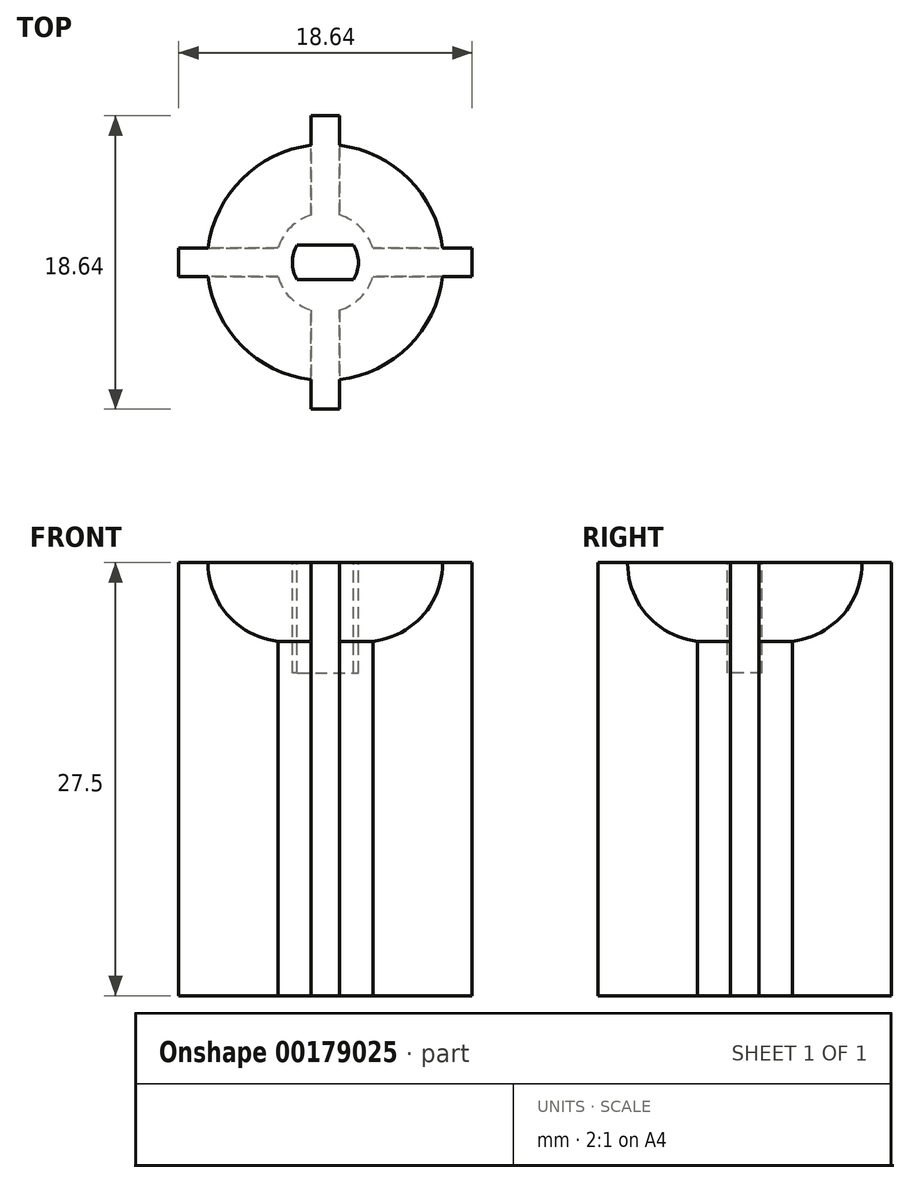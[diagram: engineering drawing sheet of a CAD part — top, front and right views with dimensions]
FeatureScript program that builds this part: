
annotation { "Feature Type Name" : "Feature", "Feature Type Description" : "" }
export const myFeature = defineFeature(function(context is Context, id is Id, definition is map)
    precondition{}
    {
        {
            var Q0;
            Q0=qCreatedBy(makeId("Top.planeOp"),FACE);
            var sketch = newSketch(context, id + "F0", { "sketchPlane" : qUnion([Q0])});
            skCircle(sketch, "E0", {"center": v(0, 0) * mm, "radius": 3.15 * mm});
            skLineSegment(sketch, "E1", {"start": v(-3.02, 0.9) * mm, "end": v(-9.32, 0.9) * mm});
            skLineSegment(sketch, "E2", {"start": v(-9.32, 0.9) * mm, "end": v(-9.32, -0.9) * mm});
            skLineSegment(sketch, "E3", {"start": v(-9.32, -0.9) * mm, "end": v(-3.02, -0.9) * mm});
            skLineSegment(sketch, "E4.1.0", {"start": v(-0.9, -3.02) * mm, "end": v(-0.9, -9.32) * mm});
            skLineSegment(sketch, "E4.1.1", {"start": v(-0.9, -9.32) * mm, "end": v(0.9, -9.32) * mm});
            skLineSegment(sketch, "E4.1.2", {"start": v(0.9, -9.32) * mm, "end": v(0.9, -3.02) * mm});
            skLineSegment(sketch, "E4.2.0", {"start": v(3.02, -0.9) * mm, "end": v(9.32, -0.9) * mm});
            skLineSegment(sketch, "E4.2.1", {"start": v(9.32, -0.9) * mm, "end": v(9.32, 0.9) * mm});
            skLineSegment(sketch, "E4.2.2", {"start": v(9.32, 0.9) * mm, "end": v(3.02, 0.9) * mm});
            skLineSegment(sketch, "E4.3.0", {"start": v(0.9, 3.02) * mm, "end": v(0.9, 9.32) * mm});
            skLineSegment(sketch, "E4.3.1", {"start": v(0.9, 9.32) * mm, "end": v(-0.9, 9.32) * mm});
            skLineSegment(sketch, "E4.3.2", {"start": v(-0.9, 9.32) * mm, "end": v(-0.9, 3.02) * mm});
            skSolve(sketch);
        }
        {
            var Q0;
            Q0=qSketchRegion(id+"F0",true);
            extrude(context, id + "F1", {"entities" : qUnion([Q0]), "depth" : 25 * mm});
        }
        {
            var Q0;
            Q0=makeQuery(id+"F1.opExtrude","CAP_FACE",FACE,{"disambiguationData":[OSD([sQuery(id+"F0.wireOp",EDGE,"E0"),sQuery(id+"F0.wireOp",EDGE,"E1"),sQuery(id+"F0.wireOp",EDGE,"E2"),sQuery(id+"F0.wireOp",EDGE,"E3"),sQuery(id+"F0.wireOp",EDGE,"3edc4b27-075a-45ef-aea2-eed3a7496e3e2.MirrorCS"),sQuery(id+"F0.wireOp",EDGE,"3edc4b27-075a-45ef-aea2-eed3a7496e3e4.MirrorCS"),sQuery(id+"F0.wireOp",EDGE,"q4PIojLU-buq7-G7pm-UIdF-VrHVZa9xzF9O")])],"isStart":false});
            var sketch = newSketch(context, id + "F2", { "sketchPlane" : qUnion([Q0])});
            skCircle(sketch, "E5", {"center": v(0, 0) * mm, "radius": 2.1 * mm});
            skLineSegment(sketch, "E6", {"start": v(-1.79, 1.1) * mm, "end": v(1.79, 1.1) * mm});
            skLineSegment(sketch, "E7", {"start": v(-1.79, -1.1) * mm, "end": v(1.79, -1.1) * mm});
            skSolve(sketch);
        }
        {
            var Q0;
            {var subQ0=sQuery(id+"F2.wireOp",EDGE,"E6");Q0=makeQuery(id+"F2.imprint","IMPRINT",FACE,{"disambiguationData":[TD([[makeQuery(id+"F2.imprint","IMPRINT",EDGE,{"derivedFrom":subQ0}),-1.0]])]});}
            extrude(context, id + "F3", {"entities" : qUnion([Q0]), "operationType" : NewBodyOperationType.REMOVE, "oppositeDirection" : true, "depth" : 7 * mm});
        }
        {
            var Q0;
            Q0=qCreatedBy(makeId("Front.planeOp"),FACE);
            cPlane(context, id + "F4", {"entities" : qUnion([Q0]), "cplaneType" : CPlaneType.OFFSET, "offset" : 3.25 * mm, "width" : 150 * mm, "height" : 150 * mm});
        }
        {
            var Q0;
            Q0=makeQuery(id+"F1.opExtrude","CAP_FACE",FACE,{"disambiguationData":[OSD([sQuery(id+"F0.wireOp",EDGE,"E0"),sQuery(id+"F0.wireOp",EDGE,"E1"),sQuery(id+"F0.wireOp",EDGE,"E2"),sQuery(id+"F0.wireOp",EDGE,"E3"),sQuery(id+"F0.wireOp",EDGE,"E4.1.0"),sQuery(id+"F0.wireOp",EDGE,"E4.1.1"),sQuery(id+"F0.wireOp",EDGE,"E4.1.2"),sQuery(id+"F0.wireOp",EDGE,"E4.2.0"),sQuery(id+"F0.wireOp",EDGE,"E4.2.1"),sQuery(id+"F0.wireOp",EDGE,"E4.2.2"),sQuery(id+"F0.wireOp",EDGE,"E4.3.0"),sQuery(id+"F0.wireOp",EDGE,"E4.3.1"),sQuery(id+"F0.wireOp",EDGE,"E4.3.2")])],"isStart":false});
            var sketch = newSketch(context, id + "F5", { "sketchPlane" : qUnion([Q0])});
            skCircle(sketch, "E8", {"center": v(0, 0) * mm, "radius": 7.5 * mm});
            skSolve(sketch);
        }
        {
            var Q0;
            {var subQ4=sQuery(id+"F0.wireOp",EDGE,"E1");var subQ7=sQuery(id+"F0.wireOp",EDGE,"E0");var subQ8=makeQuery(id+"F1.opExtrude","CAP_EDGE",EDGE,{"disambiguationData":[OSD([subQ7]),TDD([makeQuery(id+"F0.imprint","IMPRINT",EDGE,{"disambiguationData":[TD([[makeQuery(id+"F0.imprint","INTERSECT",VERTEX,{"derivedFrom":[subQ7,subQ4]}),1.0]])],"derivedFrom":subQ7})])],"isStart":false});Q0=makeQuery(id+"F5.imprint","IMPRINT",FACE,{"disambiguationData":[TD([[makeQuery(id+"F5.imprint","IMPRINT",EDGE,{"derivedFrom":subQ8}),-1.0]])]});}
            var Q1;
            {var subQ1=sQuery(id+"F0.wireOp",EDGE,"E3");var subQ7=sQuery(id+"F0.wireOp",EDGE,"E0");var subQ8=makeQuery(id+"F1.opExtrude","CAP_EDGE",EDGE,{"disambiguationData":[OSD([subQ7]),TDD([makeQuery(id+"F0.imprint","IMPRINT",EDGE,{"disambiguationData":[TD([[makeQuery(id+"F0.imprint","INTERSECT",VERTEX,{"derivedFrom":[subQ7,subQ1]}),-1.0]])],"derivedFrom":subQ7})])],"isStart":false});Q1=makeQuery(id+"F5.imprint","IMPRINT",FACE,{"disambiguationData":[TD([[makeQuery(id+"F5.imprint","IMPRINT",EDGE,{"derivedFrom":subQ8}),-1.0]])]});}
            var Q2;
            {var subQ1=sQuery(id+"F0.wireOp",EDGE,"E4.1.2");var subQ7=sQuery(id+"F0.wireOp",EDGE,"E0");var subQ8=makeQuery(id+"F1.opExtrude","CAP_EDGE",EDGE,{"disambiguationData":[OSD([subQ7]),TDD([makeQuery(id+"F0.imprint","IMPRINT",EDGE,{"disambiguationData":[TD([[makeQuery(id+"F0.imprint","INTERSECT",VERTEX,{"derivedFrom":[subQ7,subQ1]}),-1.0]])],"derivedFrom":subQ7})])],"isStart":false});Q2=makeQuery(id+"F5.imprint","IMPRINT",FACE,{"disambiguationData":[TD([[makeQuery(id+"F5.imprint","IMPRINT",EDGE,{"derivedFrom":subQ8}),-1.0]])]});}
            var Q3;
            {var subQ4=sQuery(id+"F0.wireOp",EDGE,"E4.2.2");var subQ7=sQuery(id+"F0.wireOp",EDGE,"E0");var subQ8=makeQuery(id+"F1.opExtrude","CAP_EDGE",EDGE,{"disambiguationData":[OSD([subQ7]),TDD([makeQuery(id+"F0.imprint","IMPRINT",EDGE,{"disambiguationData":[TD([[makeQuery(id+"F0.imprint","INTERSECT",VERTEX,{"derivedFrom":[subQ7,subQ4]}),-1.0]])],"derivedFrom":subQ7})])],"isStart":false});Q3=makeQuery(id+"F5.imprint","IMPRINT",FACE,{"disambiguationData":[TD([[makeQuery(id+"F5.imprint","IMPRINT",EDGE,{"derivedFrom":subQ8}),-1.0]])]});}
            extrude(context, id + "F6", {"entities" : qUnion([Q0, Q1, Q2, Q3]), "operationType" : NewBodyOperationType.ADD, "oppositeDirection" : true, "depth" : 5 * mm});
        }
        {
            var Q0;
            Q0=makeQuery(id+"F1.opExtrude","CAP_FACE",FACE,{"disambiguationData":[OSD([sQuery(id+"F0.wireOp",EDGE,"E0"),sQuery(id+"F0.wireOp",EDGE,"E1"),sQuery(id+"F0.wireOp",EDGE,"E2"),sQuery(id+"F0.wireOp",EDGE,"E3"),sQuery(id+"F0.wireOp",EDGE,"E4.1.0"),sQuery(id+"F0.wireOp",EDGE,"E4.1.1"),sQuery(id+"F0.wireOp",EDGE,"E4.1.2"),sQuery(id+"F0.wireOp",EDGE,"E4.2.0"),sQuery(id+"F0.wireOp",EDGE,"E4.2.1"),sQuery(id+"F0.wireOp",EDGE,"E4.2.2"),sQuery(id+"F0.wireOp",EDGE,"E4.3.0"),sQuery(id+"F0.wireOp",EDGE,"E4.3.1"),sQuery(id+"F0.wireOp",EDGE,"E4.3.2")])],"isStart":true});
            extrude(context, id + "F7", {"entities" : qUnion([Q0]), "operationType" : NewBodyOperationType.ADD, "depth" : 2.5 * mm});
        }
        {
            var Q0;
            {var subQ0=sQuery(id+"F5.wireOp",EDGE,"E8");Q0=makeQuery(id+"F6.opExtrude","CAP_EDGE",EDGE,{"disambiguationData":[OSD([subQ0]),TDD([makeQuery(id+"F5.imprint","IMPRINT",EDGE,{"disambiguationData":[TD([[makeQuery(id+"F5.imprint","INTERSECT",VERTEX,{"derivedFrom":[makeQuery(id+"F1.opExtrude","CAP_EDGE",EDGE,{"disambiguationData":[OSD([sQuery(id+"F0.wireOp",EDGE,"E4.3.2")])],"isStart":false}),subQ0]}),-1.0]])],"derivedFrom":subQ0})])],"isStart":false});}
            var Q1;
            {var subQ0=sQuery(id+"F5.wireOp",EDGE,"E8");Q1=makeQuery(id+"F6.opExtrude","CAP_EDGE",EDGE,{"disambiguationData":[OSD([subQ0]),TDD([makeQuery(id+"F5.imprint","IMPRINT",EDGE,{"disambiguationData":[TD([[makeQuery(id+"F5.imprint","INTERSECT",VERTEX,{"derivedFrom":[makeQuery(id+"F1.opExtrude","CAP_EDGE",EDGE,{"disambiguationData":[OSD([sQuery(id+"F0.wireOp",EDGE,"E4.3.0")])],"isStart":false}),subQ0]}),1.0]])],"derivedFrom":subQ0})])],"isStart":false});}
            var Q2;
            {var subQ0=sQuery(id+"F5.wireOp",EDGE,"E8");Q2=makeQuery(id+"F6.opExtrude","CAP_EDGE",EDGE,{"disambiguationData":[OSD([subQ0]),TDD([makeQuery(id+"F5.imprint","IMPRINT",EDGE,{"disambiguationData":[TD([[makeQuery(id+"F5.imprint","INTERSECT",VERTEX,{"derivedFrom":[makeQuery(id+"F1.opExtrude","CAP_EDGE",EDGE,{"disambiguationData":[OSD([sQuery(id+"F0.wireOp",EDGE,"E3")])],"isStart":false}),subQ0]}),-1.0]])],"derivedFrom":subQ0})])],"isStart":false});}
            var Q3;
            {var subQ0=sQuery(id+"F5.wireOp",EDGE,"E8");Q3=makeQuery(id+"F6.opExtrude","CAP_EDGE",EDGE,{"disambiguationData":[OSD([subQ0]),TDD([makeQuery(id+"F5.imprint","IMPRINT",EDGE,{"disambiguationData":[TD([[makeQuery(id+"F5.imprint","INTERSECT",VERTEX,{"derivedFrom":[makeQuery(id+"F1.opExtrude","CAP_EDGE",EDGE,{"disambiguationData":[OSD([sQuery(id+"F0.wireOp",EDGE,"E4.1.2")])],"isStart":false}),subQ0]}),-1.0]])],"derivedFrom":subQ0})])],"isStart":false});}
            fillet(context, id + "F8", {"entities" : qUnion([Q0, Q1, Q2, Q3]), "radius" : 5 * mm, "tangentPropagation" : true, "allowEdgeOverflow" : false});
        }
    });
